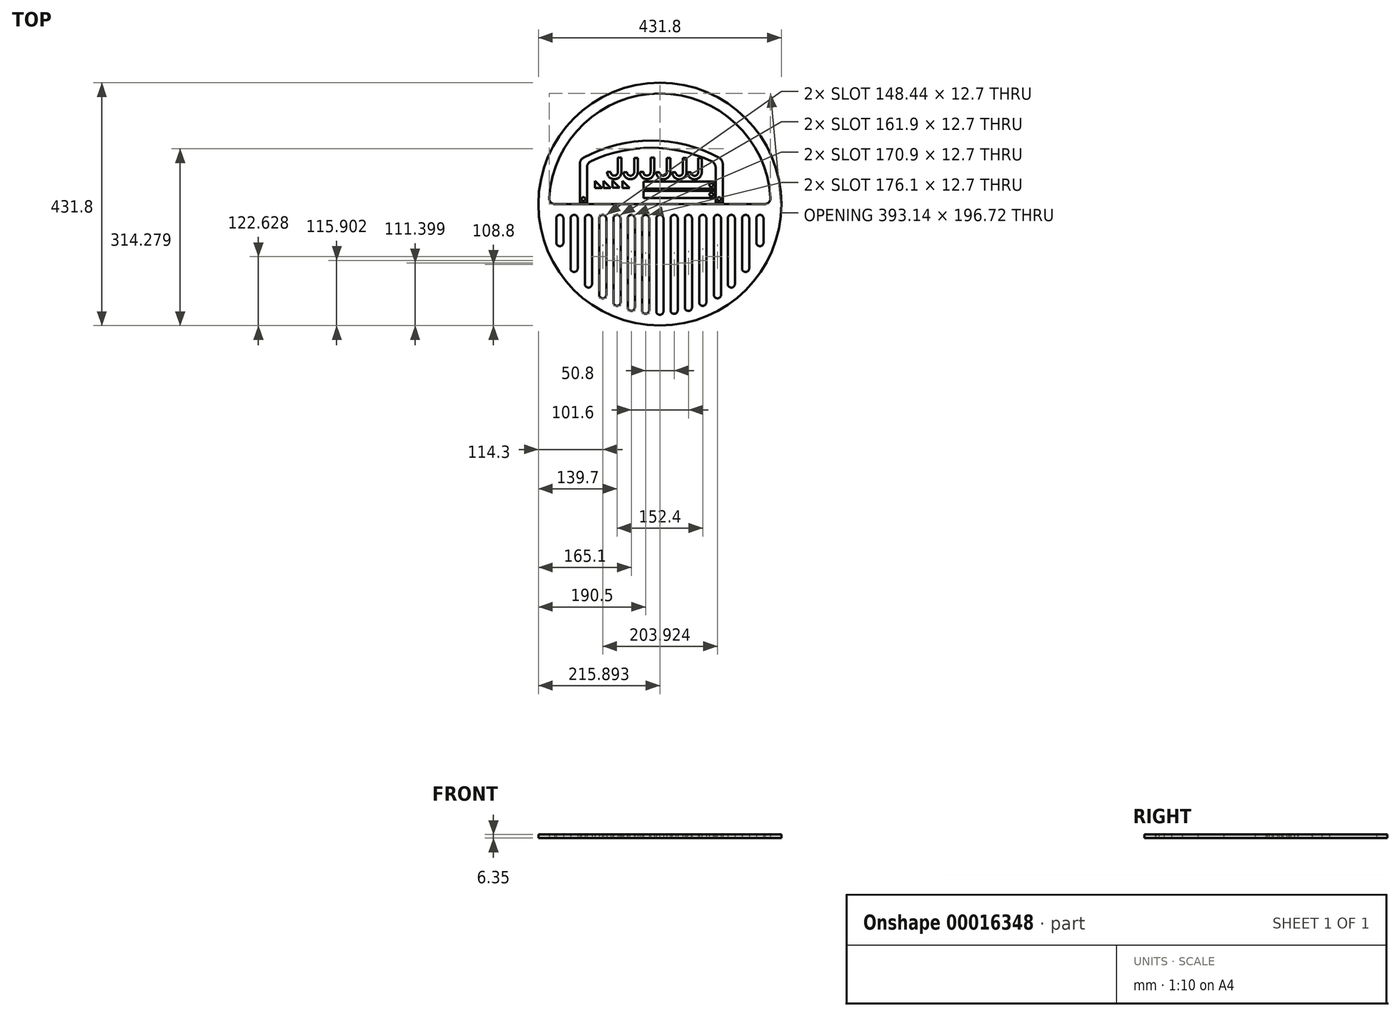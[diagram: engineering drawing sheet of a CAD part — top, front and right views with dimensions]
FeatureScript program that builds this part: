
annotation { "Feature Type Name" : "Feature", "Feature Type Description" : "" }
export const myFeature = defineFeature(function(context is Context, id is Id, definition is map)
    precondition{}
    {
        {
            var Q0;
            Q0=qCreatedBy(makeId("Top.planeOp"),FACE);
            var sketch = newSketch(context, id + "F0", { "sketchPlane" : qUnion([Q0])});
            skCircle(sketch, "E0", {"center": v(0, 0) * mm, "radius": 215.9 * mm});
            skArc(sketch, "E1", {"start": v(-146.05, -25.4) * mm, "mid": v(-152.4, -19.05) * mm, "end": v(-158.75, -25.4) * mm});
            skArc(sketch, "E2", {"start": v(-120.65, -25.4) * mm, "mid": v(-127, -19.05) * mm, "end": v(-133.35, -25.4) * mm});
            skArc(sketch, "E3", {"start": v(-95.25, -25.4) * mm, "mid": v(-101.6, -19.05) * mm, "end": v(-107.95, -25.4) * mm});
            skArc(sketch, "E4", {"start": v(-69.85, -25.4) * mm, "mid": v(-76.2, -19.05) * mm, "end": v(-82.55, -25.4) * mm});
            skArc(sketch, "E5", {"start": v(-44.45, -25.4) * mm, "mid": v(-50.8, -19.05) * mm, "end": v(-57.15, -25.4) * mm});
            skArc(sketch, "E6", {"start": v(-19.05, -25.4) * mm, "mid": v(-25.4, -19.05) * mm, "end": v(-31.75, -25.4) * mm});
            skArc(sketch, "E7", {"start": v(6.35, -25.4) * mm, "mid": v(0, -19.05) * mm, "end": v(-6.35, -25.4) * mm});
            skArc(sketch, "E8", {"start": v(31.75, -25.4) * mm, "mid": v(25.4, -19.05) * mm, "end": v(19.05, -25.4) * mm});
            skArc(sketch, "E9", {"start": v(57.15, -25.4) * mm, "mid": v(50.8, -19.05) * mm, "end": v(44.45, -25.4) * mm});
            skArc(sketch, "E10", {"start": v(82.55, -25.4) * mm, "mid": v(76.2, -19.05) * mm, "end": v(69.85, -25.4) * mm});
            skArc(sketch, "E11", {"start": v(108.67, -25.4) * mm, "mid": v(102.32, -19.05) * mm, "end": v(95.97, -25.4) * mm});
            skArc(sketch, "E12", {"start": v(133.35, -25.4) * mm, "mid": v(127, -19.05) * mm, "end": v(120.65, -25.4) * mm});
            skArc(sketch, "E13", {"start": v(158.75, -25.4) * mm, "mid": v(152.4, -19.05) * mm, "end": v(146.05, -25.4) * mm});
            skArc(sketch, "E14", {"start": v(146.05, -114.3) * mm, "mid": v(152.4, -120.65) * mm, "end": v(158.75, -114.3) * mm});
            skArc(sketch, "E15", {"start": v(120.65, -142) * mm, "mid": v(127, -148.34) * mm, "end": v(133.35, -142) * mm});
            skArc(sketch, "E16", {"start": v(95.97, -161.14) * mm, "mid": v(102.32, -167.5) * mm, "end": v(108.67, -161.14) * mm});
            skArc(sketch, "E17", {"start": v(69.85, -174.6) * mm, "mid": v(76.2, -180.95) * mm, "end": v(82.55, -174.6) * mm});
            skArc(sketch, "E18", {"start": v(44.45, -183.6) * mm, "mid": v(50.8, -189.95) * mm, "end": v(57.15, -183.6) * mm});
            skArc(sketch, "E19", {"start": v(19.05, -188.8) * mm, "mid": v(25.4, -195.15) * mm, "end": v(31.75, -188.8) * mm});
            skArc(sketch, "E20", {"start": v(-6.35, -190.5) * mm, "mid": v(0, -196.85) * mm, "end": v(6.35, -190.5) * mm});
            skArc(sketch, "E21", {"start": v(-31.75, -188.8) * mm, "mid": v(-25.4, -195.15) * mm, "end": v(-19.05, -188.8) * mm});
            skArc(sketch, "E22", {"start": v(-57.15, -183.6) * mm, "mid": v(-50.8, -189.95) * mm, "end": v(-44.45, -183.6) * mm});
            skArc(sketch, "E23", {"start": v(-82.55, -174.6) * mm, "mid": v(-76.2, -180.95) * mm, "end": v(-69.85, -174.6) * mm});
            skArc(sketch, "E24", {"start": v(-107.95, -161.14) * mm, "mid": v(-101.6, -167.5) * mm, "end": v(-95.25, -161.14) * mm});
            skArc(sketch, "E25", {"start": v(-133.35, -142) * mm, "mid": v(-127, -148.34) * mm, "end": v(-120.65, -142) * mm});
            skArc(sketch, "E26", {"start": v(-158.75, -114.3) * mm, "mid": v(-152.4, -120.65) * mm, "end": v(-146.05, -114.3) * mm});
            skLineSegment(sketch, "E27", {"start": v(-158.75, -25.4) * mm, "end": v(-158.75, -114.3) * mm});
            skLineSegment(sketch, "E28", {"start": v(-146.05, -114.3) * mm, "end": v(-146.05, -25.4) * mm});
            skLineSegment(sketch, "E29", {"start": v(-133.35, -25.4) * mm, "end": v(-133.35, -142) * mm});
            skLineSegment(sketch, "E30", {"start": v(-120.65, -142) * mm, "end": v(-120.65, -25.4) * mm});
            skLineSegment(sketch, "E31", {"start": v(-107.95, -25.4) * mm, "end": v(-107.95, -161.14) * mm});
            skLineSegment(sketch, "E32", {"start": v(-95.25, -161.14) * mm, "end": v(-95.25, -25.4) * mm});
            skLineSegment(sketch, "E33", {"start": v(-82.55, -25.4) * mm, "end": v(-82.55, -174.6) * mm});
            skLineSegment(sketch, "E34", {"start": v(-69.85, -174.6) * mm, "end": v(-69.85, -25.4) * mm});
            skLineSegment(sketch, "E35", {"start": v(-57.15, -25.4) * mm, "end": v(-57.15, -183.6) * mm});
            skLineSegment(sketch, "E36", {"start": v(-44.45, -183.6) * mm, "end": v(-44.45, -25.4) * mm});
            skLineSegment(sketch, "E37", {"start": v(-31.75, -25.4) * mm, "end": v(-31.75, -188.8) * mm});
            skLineSegment(sketch, "E38", {"start": v(-19.05, -188.8) * mm, "end": v(-19.05, -25.4) * mm});
            skLineSegment(sketch, "E39", {"start": v(-6.35, -25.4) * mm, "end": v(-6.35, -190.5) * mm});
            skLineSegment(sketch, "E40", {"start": v(6.35, -190.5) * mm, "end": v(6.35, -25.4) * mm});
            skLineSegment(sketch, "E41", {"start": v(19.05, -25.4) * mm, "end": v(19.05, -188.8) * mm});
            skLineSegment(sketch, "E42", {"start": v(31.75, -188.8) * mm, "end": v(31.75, -25.4) * mm});
            skLineSegment(sketch, "E43", {"start": v(44.45, -25.4) * mm, "end": v(44.45, -183.6) * mm});
            skLineSegment(sketch, "E44", {"start": v(57.15, -183.6) * mm, "end": v(57.15, -25.4) * mm});
            skLineSegment(sketch, "E45", {"start": v(69.85, -25.4) * mm, "end": v(69.85, -174.6) * mm});
            skLineSegment(sketch, "E46", {"start": v(82.55, -174.6) * mm, "end": v(82.55, -25.4) * mm});
            skLineSegment(sketch, "E47", {"start": v(95.97, -25.4) * mm, "end": v(95.97, -161.14) * mm});
            skLineSegment(sketch, "E48", {"start": v(108.67, -161.14) * mm, "end": v(108.67, -25.4) * mm});
            skLineSegment(sketch, "E49", {"start": v(120.65, -25.4) * mm, "end": v(120.65, -142) * mm});
            skLineSegment(sketch, "E50", {"start": v(133.35, -142) * mm, "end": v(133.35, -25.4) * mm});
            skLineSegment(sketch, "E51", {"start": v(146.05, -25.4) * mm, "end": v(146.05, -114.3) * mm});
            skLineSegment(sketch, "E52", {"start": v(158.75, -114.3) * mm, "end": v(158.75, -25.4) * mm});
            skArc(sketch, "E53", {"start": v(184.15, -25.4) * mm, "mid": v(177.8, -19.05) * mm, "end": v(171.45, -25.4) * mm});
            skLineSegment(sketch, "E54", {"start": v(171.45, -25.4) * mm, "end": v(171.45, -68.4) * mm});
            skLineSegment(sketch, "E55", {"start": v(184.15, -25.4) * mm, "end": v(184.15, -68.4) * mm});
            skArc(sketch, "E56", {"start": v(171.45, -68.4) * mm, "mid": v(177.8, -74.74) * mm, "end": v(184.15, -68.4) * mm});
            skArc(sketch, "E57.MirrorCS", {"start": v(-184.15, -25.4) * mm, "mid": v(-177.8, -19.06) * mm, "end": v(-171.45, -25.4) * mm});
            skLineSegment(sketch, "E58.MirrorCS", {"start": v(-171.45, -25.4) * mm, "end": v(-171.45, -68.4) * mm});
            skLineSegment(sketch, "E59.MirrorCS", {"start": v(-184.15, -25.4) * mm, "end": v(-184.15, -68.4) * mm});
            skArc(sketch, "E60.MirrorCS", {"start": v(-171.45, -68.4) * mm, "mid": v(-177.8, -74.75) * mm, "end": v(-184.15, -68.4) * mm});
            skArc(sketch, "E61", {"start": v(-196.53, 11.3) * mm, "mid": v(-194.28, 3.6) * mm, "end": v(-187.12, 0.02) * mm});
            skArc(sketch, "E62.MirrorCS", {"start": v(196.5, 11.52) * mm, "mid": v(194.28, 3.83) * mm, "end": v(187.12, 0.24) * mm});
            skArc(sketch, "E63", {"start": v(196.5, 11.52) * mm, "mid": v(-0.12, 196.74) * mm, "end": v(-196.53, 11.3) * mm});
            skLineSegment(sketch, "E64", {"start": v(-187.12, 0.02) * mm, "end": v(187.12, 0.24) * mm});
            skLineSegment(sketch, "E65", {"start": v(-100.32, 28.62) * mm, "end": v(-87.62, 28.62) * mm});
            skLineSegment(sketch, "E66", {"start": v(-87.62, 28.62) * mm, "end": v(-100.32, 41.32) * mm});
            skLineSegment(sketch, "E67", {"start": v(-100.32, 41.32) * mm, "end": v(-100.32, 28.62) * mm});
            skLineSegment(sketch, "E68", {"start": v(-71.38, 29.12) * mm, "end": v(-84.08, 41.82) * mm});
            skLineSegment(sketch, "E69", {"start": v(-84.08, 29.12) * mm, "end": v(-71.38, 29.12) * mm});
            skLineSegment(sketch, "E70", {"start": v(-84.08, 41.82) * mm, "end": v(-84.08, 29.12) * mm});
            skLineSegment(sketch, "E71", {"start": v(-53.53, 28.87) * mm, "end": v(-66.23, 41.57) * mm});
            skLineSegment(sketch, "E72", {"start": v(-66.23, 28.87) * mm, "end": v(-53.53, 28.87) * mm});
            skLineSegment(sketch, "E73", {"start": v(-66.23, 41.57) * mm, "end": v(-66.23, 28.87) * mm});
            skLineSegment(sketch, "E74", {"start": v(-115.2, 41.45) * mm, "end": v(-115.2, 28.75) * mm});
            skLineSegment(sketch, "E75", {"start": v(-102.5, 28.75) * mm, "end": v(-115.2, 41.45) * mm});
            skLineSegment(sketch, "E76", {"start": v(-115.2, 28.75) * mm, "end": v(-102.5, 28.75) * mm});
            skPoint(sketch, "E77", {"position": v(-142.28, 78.88) * mm});
            skPoint(sketch, "E78", {"position": v(111.72, 78.88) * mm});
            skArc(sketch, "E79", {"start": v(105.06, 82.61) * mm, "mid": v(-15.28, 113.02) * mm, "end": v(-135.61, 82.6) * mm});
            skLineSegment(sketch, "E80", {"start": v(-142.28, 2.68) * mm, "end": v(-129.58, 2.68) * mm});
            skLineSegment(sketch, "E81", {"start": v(-129.58, 2.68) * mm, "end": v(-129.58, 65.07) * mm});
            skLineSegment(sketch, "E82.MirrorCS", {"start": v(99.02, 2.68) * mm, "end": v(99.02, 64.9) * mm});
            skLineSegment(sketch, "E83.MirrorCS", {"start": v(111.72, 2.68) * mm, "end": v(99.02, 2.68) * mm});
            skArc(sketch, "E84", {"start": v(91.68, 76.41) * mm, "mid": v(-15.25, 100.12) * mm, "end": v(-122.22, 76.6) * mm});
            skPoint(sketch, "E85.visualSharp", {"position": v(-129.58, 73.04) * mm});
            skArc(sketch, "E85.filletArc", {"start": v(-122.22, 76.6) * mm, "mid": v(-127.58, 71.9) * mm, "end": v(-129.58, 65.07) * mm});
            skPoint(sketch, "E86.visualSharp", {"position": v(99.02, 72.85) * mm});
            skArc(sketch, "E86.filletArc", {"start": v(99.02, 64.9) * mm, "mid": v(97.03, 71.73) * mm, "end": v(91.68, 76.41) * mm});
            skArc(sketch, "E87.filletArc", {"start": v(111.72, 71.44) * mm, "mid": v(109.93, 77.94) * mm, "end": v(105.06, 82.61) * mm});
            skArc(sketch, "E88.filletArc", {"start": v(-135.61, 82.6) * mm, "mid": v(-140.48, 77.94) * mm, "end": v(-142.28, 71.43) * mm});
            skLineSegment(sketch, "E89", {"start": v(-142.28, 71.43) * mm, "end": v(-142.28, 2.68) * mm});
            skLineSegment(sketch, "E90", {"start": v(111.72, 71.44) * mm, "end": v(111.72, 2.68) * mm});
            skCircle(sketch, "E91", {"center": v(105.37, 9.03) * mm, "radius": 3.3 * mm});
            skCircle(sketch, "E92.MirrorC", {"center": v(-135.93, 9.03) * mm, "radius": 3.3 * mm});
            skLineSegment(sketch, "E93", {"start": v(-74.68, 82.4) * mm, "end": v(-68.33, 82.4) * mm});
            skLineSegment(sketch, "E94", {"start": v(-68.33, 82.4) * mm, "end": v(-68.33, 57) * mm});
            skLineSegment(sketch, "E95", {"start": v(-74.68, 82.4) * mm, "end": v(-74.68, 57) * mm});
            skArc(sketch, "E96", {"start": v(-87.38, 57) * mm, "mid": v(-81.03, 50.66) * mm, "end": v(-74.68, 57) * mm});
            skLineSegment(sketch, "E97", {"start": v(-87.38, 57) * mm, "end": v(-93.73, 57) * mm});
            skArc(sketch, "E98", {"start": v(-93.73, 57) * mm, "mid": v(-81.03, 44.3) * mm, "end": v(-68.33, 57) * mm});
            skLineSegment(sketch, "E99", {"start": v(-45.8, 82.29) * mm, "end": v(-39.46, 82.29) * mm});
            skLineSegment(sketch, "E100", {"start": v(-45.8, 82.29) * mm, "end": v(-45.8, 56.89) * mm});
            skLineSegment(sketch, "E101", {"start": v(-39.46, 82.29) * mm, "end": v(-39.46, 56.89) * mm});
            skArc(sketch, "E102", {"start": v(-58.5, 56.89) * mm, "mid": v(-52.16, 50.54) * mm, "end": v(-45.8, 56.89) * mm});
            skLineSegment(sketch, "E103", {"start": v(-58.5, 56.89) * mm, "end": v(-64.86, 56.89) * mm});
            skArc(sketch, "E104", {"start": v(-64.86, 56.89) * mm, "mid": v(-52.16, 44.19) * mm, "end": v(-39.46, 56.89) * mm});
            skLineSegment(sketch, "E105", {"start": v(-16.63, 82.48) * mm, "end": v(-10.28, 82.48) * mm});
            skLineSegment(sketch, "E106", {"start": v(-16.63, 82.48) * mm, "end": v(-16.63, 57.08) * mm});
            skLineSegment(sketch, "E107", {"start": v(-10.28, 82.48) * mm, "end": v(-10.28, 57.08) * mm});
            skArc(sketch, "E108", {"start": v(-29.33, 57.08) * mm, "mid": v(-22.98, 50.73) * mm, "end": v(-16.63, 57.08) * mm});
            skLineSegment(sketch, "E109", {"start": v(-29.33, 57.08) * mm, "end": v(-35.68, 57.08) * mm});
            skArc(sketch, "E110", {"start": v(-35.68, 57.08) * mm, "mid": v(-22.98, 44.38) * mm, "end": v(-10.28, 57.08) * mm});
            skLineSegment(sketch, "E111", {"start": v(12.36, 82.29) * mm, "end": v(18.7, 82.29) * mm});
            skLineSegment(sketch, "E112", {"start": v(12.36, 82.29) * mm, "end": v(12.36, 56.89) * mm});
            skLineSegment(sketch, "E113", {"start": v(18.7, 82.29) * mm, "end": v(18.7, 56.89) * mm});
            skArc(sketch, "E114", {"start": v(-0.34, 56.89) * mm, "mid": v(6, 50.54) * mm, "end": v(12.36, 56.89) * mm});
            skLineSegment(sketch, "E115", {"start": v(-0.34, 56.89) * mm, "end": v(-6.7, 56.89) * mm});
            skArc(sketch, "E116", {"start": v(-6.7, 56.89) * mm, "mid": v(6, 44.19) * mm, "end": v(18.7, 56.89) * mm});
            skLineSegment(sketch, "E117", {"start": v(40.96, 82.1) * mm, "end": v(47.31, 82.1) * mm});
            skLineSegment(sketch, "E118", {"start": v(40.96, 82.1) * mm, "end": v(40.96, 56.7) * mm});
            skLineSegment(sketch, "E119", {"start": v(47.31, 82.1) * mm, "end": v(47.31, 56.7) * mm});
            skArc(sketch, "E120", {"start": v(28.26, 56.7) * mm, "mid": v(34.61, 50.35) * mm, "end": v(40.96, 56.7) * mm});
            skLineSegment(sketch, "E121", {"start": v(28.26, 56.7) * mm, "end": v(21.91, 56.7) * mm});
            skArc(sketch, "E122", {"start": v(21.91, 56.7) * mm, "mid": v(34.61, 44) * mm, "end": v(47.31, 56.7) * mm});
            skLineSegment(sketch, "E123.bottom", {"start": v(97.78, 10.73) * mm, "end": v(-29.22, 10.73) * mm});
            skLineSegment(sketch, "E123.top", {"start": v(97.78, 23.43) * mm, "end": v(-29.22, 23.43) * mm});
            skLineSegment(sketch, "E123.left", {"start": v(97.78, 10.73) * mm, "end": v(97.78, 23.43) * mm});
            skLineSegment(sketch, "E123.right", {"start": v(-29.22, 10.73) * mm, "end": v(-29.22, 23.43) * mm});
            skLineSegment(sketch, "E124.bottom", {"start": v(97.78, 27.62) * mm, "end": v(-29.22, 27.62) * mm});
            skLineSegment(sketch, "E124.top", {"start": v(97.78, 40.32) * mm, "end": v(-29.22, 40.32) * mm});
            skLineSegment(sketch, "E124.left", {"start": v(97.78, 27.62) * mm, "end": v(97.78, 40.32) * mm});
            skLineSegment(sketch, "E124.right", {"start": v(-29.22, 27.62) * mm, "end": v(-29.22, 40.32) * mm});
            skPoint(sketch, "E125", {"position": v(97.78, 33.97) * mm});
            skPoint(sketch, "E126", {"position": v(91.43, 40.32) * mm});
            skPoint(sketch, "E127", {"position": v(91.43, 23.43) * mm});
            skPoint(sketch, "E128", {"position": v(97.78, 17.08) * mm});
            skCircle(sketch, "E129", {"center": v(91.43, 33.97) * mm, "radius": 3.3 * mm});
            skCircle(sketch, "E130", {"center": v(91.43, 17.08) * mm, "radius": 3.3 * mm});
            skArc(sketch, "E131", {"start": v(49, 56.67) * mm, "mid": v(61.7, 43.97) * mm, "end": v(74.4, 56.67) * mm});
            skLineSegment(sketch, "E132", {"start": v(55.35, 56.67) * mm, "end": v(49, 56.67) * mm});
            skArc(sketch, "E133", {"start": v(55.35, 56.67) * mm, "mid": v(61.7, 50.32) * mm, "end": v(68.05, 56.67) * mm});
            skLineSegment(sketch, "E134", {"start": v(74.4, 82.07) * mm, "end": v(74.4, 56.67) * mm});
            skLineSegment(sketch, "E135", {"start": v(68.05, 82.07) * mm, "end": v(68.05, 56.67) * mm});
            skLineSegment(sketch, "E136", {"start": v(68.05, 82.07) * mm, "end": v(74.4, 82.07) * mm});
            skSolve(sketch);
        }
        {
            var Q0;
            Q0=makeQuery(id+"F0.imprint","IMPRINT",FACE,{"disambiguationData":[TD([[makeQuery(id+"F0.imprint","IMPRINT",EDGE,{"derivedFrom":sQuery(id+"F0.wireOp",EDGE,"E0")}),1.0]])]});
            var Q1;
            Q1=makeQuery(id+"F0.imprint","IMPRINT",FACE,{"disambiguationData":[TD([[makeQuery(id+"F0.imprint","IMPRINT",EDGE,{"derivedFrom":sQuery(id+"F0.wireOp",EDGE,"E79")}),1.0]])]});
            var Q2;
            Q2=makeQuery(id+"F0.imprint","IMPRINT",FACE,{"disambiguationData":[TD([[makeQuery(id+"F0.imprint","IMPRINT",EDGE,{"derivedFrom":sQuery(id+"F0.wireOp",EDGE,"E74")}),1.0]])]});
            var Q3;
            Q3=makeQuery(id+"F0.imprint","IMPRINT",FACE,{"disambiguationData":[TD([[makeQuery(id+"F0.imprint","IMPRINT",EDGE,{"derivedFrom":sQuery(id+"F0.wireOp",EDGE,"E65")}),1.0]])]});
            var Q4;
            Q4=makeQuery(id+"F0.imprint","IMPRINT",FACE,{"disambiguationData":[TD([[makeQuery(id+"F0.imprint","IMPRINT",EDGE,{"derivedFrom":sQuery(id+"F0.wireOp",EDGE,"E68")}),1.0]])]});
            var Q5;
            Q5=makeQuery(id+"F0.imprint","IMPRINT",FACE,{"disambiguationData":[TD([[makeQuery(id+"F0.imprint","IMPRINT",EDGE,{"derivedFrom":sQuery(id+"F0.wireOp",EDGE,"E71")}),1.0]])]});
            var Q6;
            Q6=makeQuery(id+"F0.imprint","IMPRINT",FACE,{"disambiguationData":[TD([[makeQuery(id+"F0.imprint","IMPRINT",EDGE,{"derivedFrom":sQuery(id+"F0.wireOp",EDGE,"E93")}),-1.0]])]});
            var Q7;
            Q7=makeQuery(id+"F0.imprint","IMPRINT",FACE,{"disambiguationData":[TD([[makeQuery(id+"F0.imprint","IMPRINT",EDGE,{"derivedFrom":sQuery(id+"F0.wireOp",EDGE,"E99")}),-1.0]])]});
            var Q8;
            Q8=makeQuery(id+"F0.imprint","IMPRINT",FACE,{"disambiguationData":[TD([[makeQuery(id+"F0.imprint","IMPRINT",EDGE,{"derivedFrom":sQuery(id+"F0.wireOp",EDGE,"E105")}),-1.0]])]});
            var Q9;
            Q9=makeQuery(id+"F0.imprint","IMPRINT",FACE,{"disambiguationData":[TD([[makeQuery(id+"F0.imprint","IMPRINT",EDGE,{"derivedFrom":sQuery(id+"F0.wireOp",EDGE,"E111")}),-1.0]])]});
            var Q10;
            Q10=makeQuery(id+"F0.imprint","IMPRINT",FACE,{"disambiguationData":[TD([[makeQuery(id+"F0.imprint","IMPRINT",EDGE,{"derivedFrom":sQuery(id+"F0.wireOp",EDGE,"E117")}),-1.0]])]});
            var Q11;
            Q11=makeQuery(id+"F0.imprint","IMPRINT",FACE,{"disambiguationData":[TD([[makeQuery(id+"F0.imprint","IMPRINT",EDGE,{"derivedFrom":sQuery(id+"F0.wireOp",EDGE,"E124.bottom")}),-1.0]])]});
            var Q12;
            Q12=makeQuery(id+"F0.imprint","IMPRINT",FACE,{"disambiguationData":[TD([[makeQuery(id+"F0.imprint","IMPRINT",EDGE,{"derivedFrom":sQuery(id+"F0.wireOp",EDGE,"E123.bottom")}),-1.0]])]});
            var Q13;
            Q13=makeQuery(id+"F0.imprint","IMPRINT",FACE,{"disambiguationData":[TD([[makeQuery(id+"F0.imprint","IMPRINT",EDGE,{"derivedFrom":sQuery(id+"F0.wireOp",EDGE,"E131")}),1.0]])]});
            extrude(context, id + "F1", {"entities" : qUnion([Q0, Q1, Q2, Q3, Q4, Q5, Q6, Q7, Q8, Q9, Q10, Q11, Q12, Q13]), "depth" : 6.35 * mm});
        }
    });
